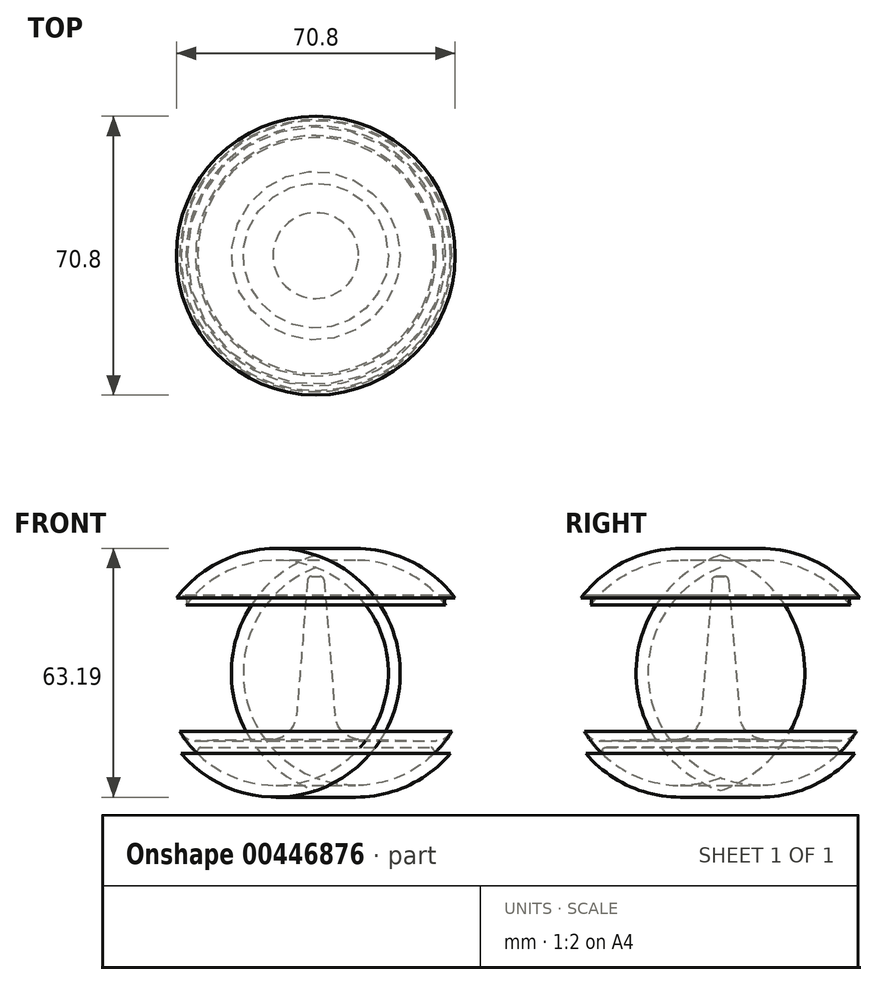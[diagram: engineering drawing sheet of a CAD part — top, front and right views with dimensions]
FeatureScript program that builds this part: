
annotation { "Feature Type Name" : "Feature", "Feature Type Description" : "" }
export const myFeature = defineFeature(function(context is Context, id is Id, definition is map)
    precondition{}
    {
        {
            var Q0;
            Q0=qCreatedBy(makeId("Front.planeOp"),FACE);
            var sketch = newSketch(context, id + "F0", { "sketchPlane" : qUnion([Q0])});
            skLineSegment(sketch, "E0", {"start": v(0, 1.5) * mm, "end": v(0, 45) * mm});
            skLineSegment(sketch, "E1", {"start": v(0, 45) * mm, "end": v(1.08, 45) * mm});
            skLineSegment(sketch, "E2", {"start": v(2.08, 44.08) * mm, "end": v(4.89, 9.66) * mm});
            skLineSegment(sketch, "E3", {"start": v(30.75, 0) * mm, "end": v(34.2, 0) * mm});
            skArc(sketch, "E4", {"start": v(34.2, 0) * mm, "mid": v(41.74, 19.54) * mm, "end": v(35.4, 39.5) * mm});
            skArc(sketch, "E5.0", {"start": v(34.56, 5.59) * mm, "mid": v(38.72, 21.88) * mm, "end": v(33, 37.7) * mm});
            skLineSegment(sketch, "E6", {"start": v(33.25, 39.76) * mm, "end": v(33.25, 39.76) * mm});
            skPoint(sketch, "E7.visualSharp", {"position": v(34.43, 40.72) * mm});
            skArc(sketch, "E7.filletArc", {"start": v(35.4, 39.5) * mm, "mid": v(34.38, 40.08) * mm, "end": v(33.25, 39.76) * mm});
            skPoint(sketch, "E8.visualSharp", {"position": v(32.11, 38.82) * mm});
            skArc(sketch, "E8.filletArc", {"start": v(33.25, 39.76) * mm, "mid": v(32.71, 38.77) * mm, "end": v(33, 37.7) * mm});
            skPoint(sketch, "E9.visualSharp", {"position": v(2, 45) * mm});
            skArc(sketch, "E9.filletArc", {"start": v(2.08, 44.08) * mm, "mid": v(1.76, 44.74) * mm, "end": v(1.08, 45) * mm});
            skPoint(sketch, "E10.visualSharp", {"position": v(5.43, 3.04) * mm});
            skPoint(sketch, "E11.visualSharp", {"position": v(33.05, 3.36) * mm});
            skArc(sketch, "E11.filletArc", {"start": v(30.52, 3.2) * mm, "mid": v(32.84, 3.9) * mm, "end": v(34.56, 5.59) * mm});
            skArc(sketch, "E12", {"start": v(4.89, 9.66) * mm, "mid": v(6.78, 5.53) * mm, "end": v(10.88, 3.57) * mm});
            skLineSegment(sketch, "E13", {"start": v(10.88, 3.57) * mm, "end": v(30.52, 3.2) * mm});
            skLineSegment(sketch, "E14", {"start": v(0, 1.5) * mm, "end": v(29.25, 1.5) * mm});
            skLineSegment(sketch, "E15", {"start": v(30, 0.75) * mm, "end": v(30, 0.75) * mm});
            skPoint(sketch, "E16.visualSharp", {"position": v(30, 1.5) * mm});
            skArc(sketch, "E16.filletArc", {"start": v(30, 0.75) * mm, "mid": v(29.78, 1.28) * mm, "end": v(29.25, 1.5) * mm});
            skPoint(sketch, "E17.newPointB", {"position": v(4.2, 0) * mm});
            skArc(sketch, "E17.filletArc", {"start": v(30, 0.75) * mm, "mid": v(30.22, 0.22) * mm, "end": v(30.75, 0) * mm});
            skSolve(sketch);
        }
        {
            var Q0;
            Q0=qCreatedBy(makeId("Top.planeOp"),FACE);
            var sketch = newSketch(context, id + "F1", { "sketchPlane" : qUnion([Q0])});
            skCircle(sketch, "E18", {"center": v(0, 0) * mm, "radius": 3.13 * mm});
            skSolve(sketch);
        }
        {
            var Q0;
            Q0=makeQuery(id+"F0.imprint","IMPRINT",FACE,{"disambiguationData":[TD([[makeQuery(id+"F0.imprint","IMPRINT",EDGE,{"derivedFrom":sQuery(id+"F0.wireOp",EDGE,"E0")}),-1.0]])]});
            var Q1;
            Q1=sQuery(id+"F1.wireOp",EDGE,"E18");
            revolve(context, id + "F2", {"entities" : qUnion([Q0]), "axis" : qUnion([Q1]), "revolveType" : RevolveType.FULL});
        }
    });
